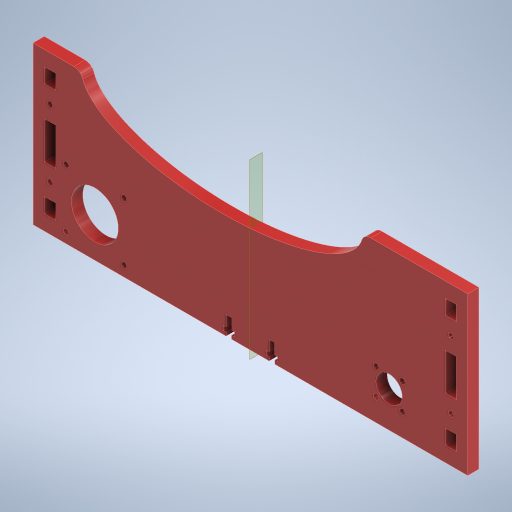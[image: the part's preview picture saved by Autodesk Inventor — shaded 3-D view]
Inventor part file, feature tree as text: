
AUTODESK INVENTOR PART (.ipt)
format: ipt  version: 2024.2 (Build 282272000, 272)  size: 417,792 bytes
history: native  units: mm
features: extrude x5, sketch x5, other x2, fillet x1, mirror x1
ambient origin geometry x8: Origin, YZ Plane, XZ Plane, XY Plane, X Axis, Y Axis, Z Axis, Center Point
bodies: Body1 (feature_tree)
feature tree (14):
  other  "Твердое тело1"
  extrude  "Выдавливание1"  Depth=6.0mm TaperAngle=0.0deg
  extrude  "Выдавливание2"  Depth=6.0mm
  other  "РабПлоскость1"
  extrude  "Выдавливание3"  Depth=8.0mm
  fillet  "Сопряжение1"  Radius=8.0mm
  extrude  "Выдавливание4"  Depth=8.0mm
  extrude  "Выдавливание5"  Depth=84.0mm
  mirror  "Зеркальное отражение2"
  sketch  "Эскиз1"
  sketch  "Эскиз2"
  sketch  "Эскиз5"
  sketch  "Эскиз6"
  sketch  "Эскиз7"
